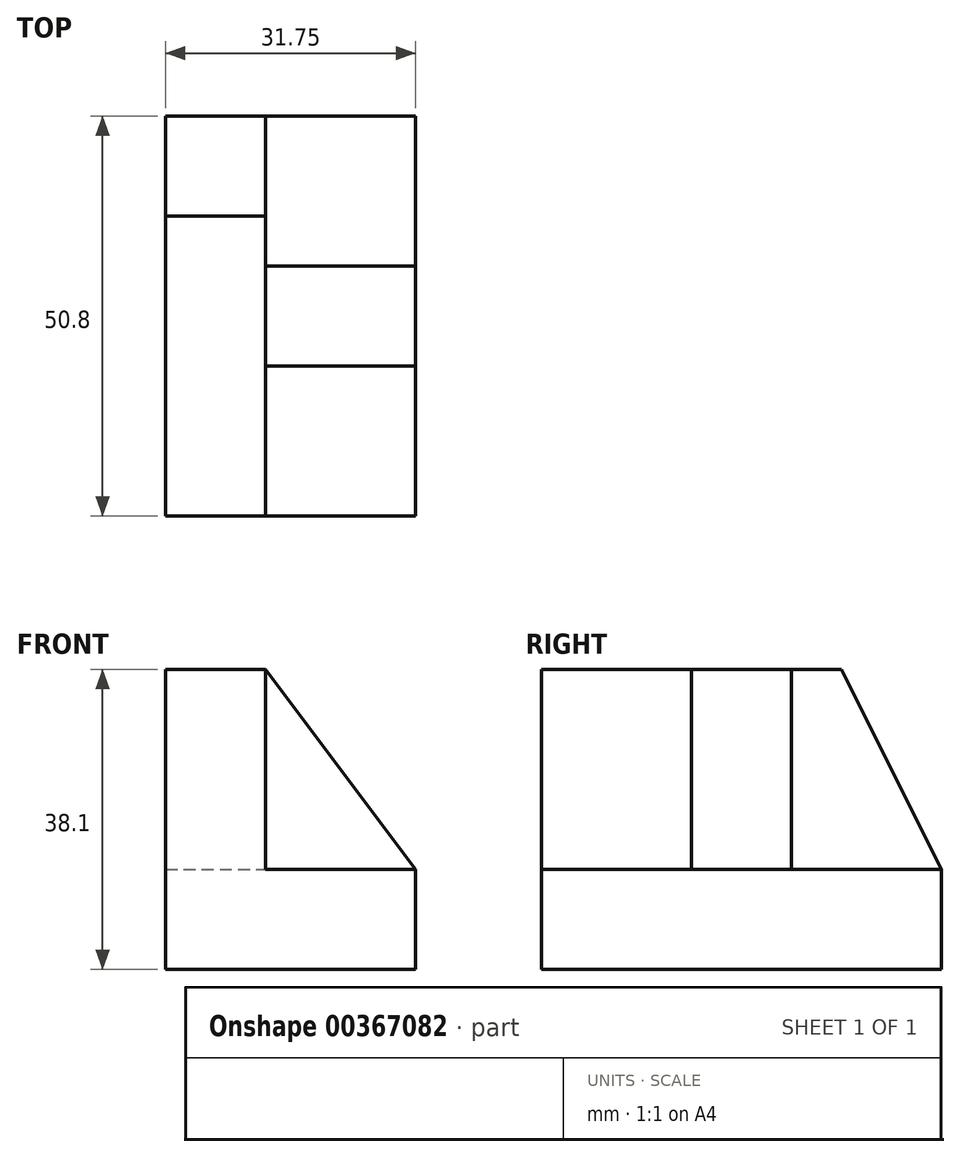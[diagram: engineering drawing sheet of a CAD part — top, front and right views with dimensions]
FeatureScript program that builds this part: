
annotation { "Feature Type Name" : "Feature", "Feature Type Description" : "" }
export const myFeature = defineFeature(function(context is Context, id is Id, definition is map)
    precondition{}
    {
        {
            var Q0;
            Q0=qCreatedBy(makeId("Right.planeOp"),FACE);
            var sketch = newSketch(context, id + "F0", { "sketchPlane" : qUnion([Q0])});
            skLineSegment(sketch, "E0.bottom", {"start": v(0, 0) * mm, "end": v(50.8, 0) * mm});
            skLineSegment(sketch, "E0.top", {"start": v(0, 38.1) * mm, "end": v(50.8, 38.1) * mm});
            skLineSegment(sketch, "E0.left", {"start": v(0, 0) * mm, "end": v(0, 38.1) * mm});
            skLineSegment(sketch, "E0.right", {"start": v(50.8, 0) * mm, "end": v(50.8, 38.1) * mm});
            skSolve(sketch);
        }
        {
            var Q0;
            Q0=makeQuery(id+"F0.imprint","IMPRINT",FACE,{"disambiguationData":[TD([[makeQuery(id+"F0.imprint","IMPRINT",EDGE,{"derivedFrom":sQuery(id+"F0.wireOp",EDGE,"E0.bottom")}),1.0]])]});
            extrude(context, id + "F1", {"entities" : qUnion([Q0]), "depth" : 31.75 * mm});
        }
        {
            var Q0;
            Q0=makeQuery(id+"F1.opExtrude","CAP_FACE",FACE,{"disambiguationData":[OSD([sQuery(id+"F0.wireOp",EDGE,"E0.bottom"),sQuery(id+"F0.wireOp",EDGE,"E0.top"),sQuery(id+"F0.wireOp",EDGE,"E0.left"),sQuery(id+"F0.wireOp",EDGE,"E0.right")])],"isStart":false});
            var sketch = newSketch(context, id + "F2", { "sketchPlane" : qUnion([Q0])});
            skLineSegment(sketch, "E1", {"start": v(50.8, 38.1) * mm, "end": v(38.1, 38.1) * mm});
            skLineSegment(sketch, "E2", {"start": v(38.1, 38.1) * mm, "end": v(50.8, 12.7) * mm});
            skLineSegment(sketch, "E3", {"start": v(50.8, 12.7) * mm, "end": v(50.8, 38.1) * mm});
            skSolve(sketch);
        }
        {
            var Q0;
            Q0=makeQuery(id+"F2.imprint","IMPRINT",FACE,{"disambiguationData":[TD([[makeQuery(id+"F2.imprint","IMPRINT",EDGE,{"derivedFrom":sQuery(id+"F2.wireOp",EDGE,"E1")}),-1.0]])]});
            extrude(context, id + "F3", {"entities" : qUnion([Q0]), "operationType" : NewBodyOperationType.REMOVE, "oppositeDirection" : true, "depth" : 31.75 * mm});
        }
        {
            var Q0;
            Q0=makeQuery(id+"F1.opExtrude","CAP_FACE",FACE,{"disambiguationData":[OSD([sQuery(id+"F0.wireOp",EDGE,"E0.bottom"),sQuery(id+"F0.wireOp",EDGE,"E0.top"),sQuery(id+"F0.wireOp",EDGE,"E0.left"),sQuery(id+"F0.wireOp",EDGE,"E0.right")])],"isStart":false});
            var sketch = newSketch(context, id + "F4", { "sketchPlane" : qUnion([Q0])});
            skLineSegment(sketch, "E4", {"start": v(50.8, 12.7) * mm, "end": v(31.75, 12.7) * mm});
            skLineSegment(sketch, "E5", {"start": v(31.75, 12.7) * mm, "end": v(31.75, 38.1) * mm});
            skLineSegment(sketch, "E6", {"start": v(31.75, 38.1) * mm, "end": v(38.1, 38.1) * mm});
            skLineSegment(sketch, "E7", {"start": v(38.1, 38.1) * mm, "end": v(50.8, 12.7) * mm});
            skSolve(sketch);
        }
        {
            var Q0;
            Q0=makeQuery(id+"F4.imprint","IMPRINT",FACE,{"disambiguationData":[TD([[makeQuery(id+"F4.imprint","IMPRINT",EDGE,{"derivedFrom":sQuery(id+"F4.wireOp",EDGE,"E4")}),-1.0]])]});
            extrude(context, id + "F5", {"entities" : qUnion([Q0]), "operationType" : NewBodyOperationType.REMOVE, "oppositeDirection" : true, "depth" : 19.05 * mm});
        }
        {
            var Q0;
            Q0=makeQuery(id+"F5.boolean.opBoolean","COPY",FACE,{"derivedFrom":makeQuery(id+"F5.opExtrude","SWEPT_FACE",FACE,{"disambiguationData":[OSD([sQuery(id+"F4.wireOp",EDGE,"E5")])]})});
            var sketch = newSketch(context, id + "F6", { "sketchPlane" : qUnion([Q0])});
            skLineSegment(sketch, "E8", {"start": v(-31.75, 12.7) * mm, "end": v(-31.75, 38.1) * mm});
            skLineSegment(sketch, "E9", {"start": v(-31.75, 38.1) * mm, "end": v(-12.7, 38.1) * mm});
            skLineSegment(sketch, "E10", {"start": v(-12.7, 38.1) * mm, "end": v(-31.75, 12.7) * mm});
            skSolve(sketch);
        }
        {
            var Q0;
            Q0=makeQuery(id+"F6.imprint","IMPRINT",FACE,{"disambiguationData":[TD([[makeQuery(id+"F6.imprint","IMPRINT",EDGE,{"derivedFrom":sQuery(id+"F6.wireOp",EDGE,"E8")}),-1.0]])]});
            extrude(context, id + "F7", {"entities" : qUnion([Q0]), "operationType" : NewBodyOperationType.REMOVE, "oppositeDirection" : true, "depth" : 12.7 * mm});
        }
        {
            var Q0;
            Q0=makeQuery(id+"F1.opExtrude","CAP_FACE",FACE,{"disambiguationData":[OSD([sQuery(id+"F0.wireOp",EDGE,"E0.bottom"),sQuery(id+"F0.wireOp",EDGE,"E0.top"),sQuery(id+"F0.wireOp",EDGE,"E0.left"),sQuery(id+"F0.wireOp",EDGE,"E0.right")])],"isStart":false});
            var sketch = newSketch(context, id + "F8", { "sketchPlane" : qUnion([Q0])});
            skLineSegment(sketch, "E11", {"start": v(19.05, 12.7) * mm, "end": v(0, 12.7) * mm});
            skLineSegment(sketch, "E12", {"start": v(0, 12.7) * mm, "end": v(0, 38.1) * mm});
            skLineSegment(sketch, "E13", {"start": v(0, 38.1) * mm, "end": v(19.05, 38.1) * mm});
            skLineSegment(sketch, "E14", {"start": v(19.05, 38.1) * mm, "end": v(19.05, 12.7) * mm});
            skSolve(sketch);
        }
        {
            var Q0;
            Q0=makeQuery(id+"F8.imprint","IMPRINT",FACE,{"disambiguationData":[TD([[makeQuery(id+"F8.imprint","IMPRINT",EDGE,{"derivedFrom":sQuery(id+"F8.wireOp",EDGE,"E11")}),-1.0]])]});
            extrude(context, id + "F9", {"entities" : qUnion([Q0]), "operationType" : NewBodyOperationType.REMOVE, "oppositeDirection" : true, "depth" : 19.05 * mm});
        }
    });
